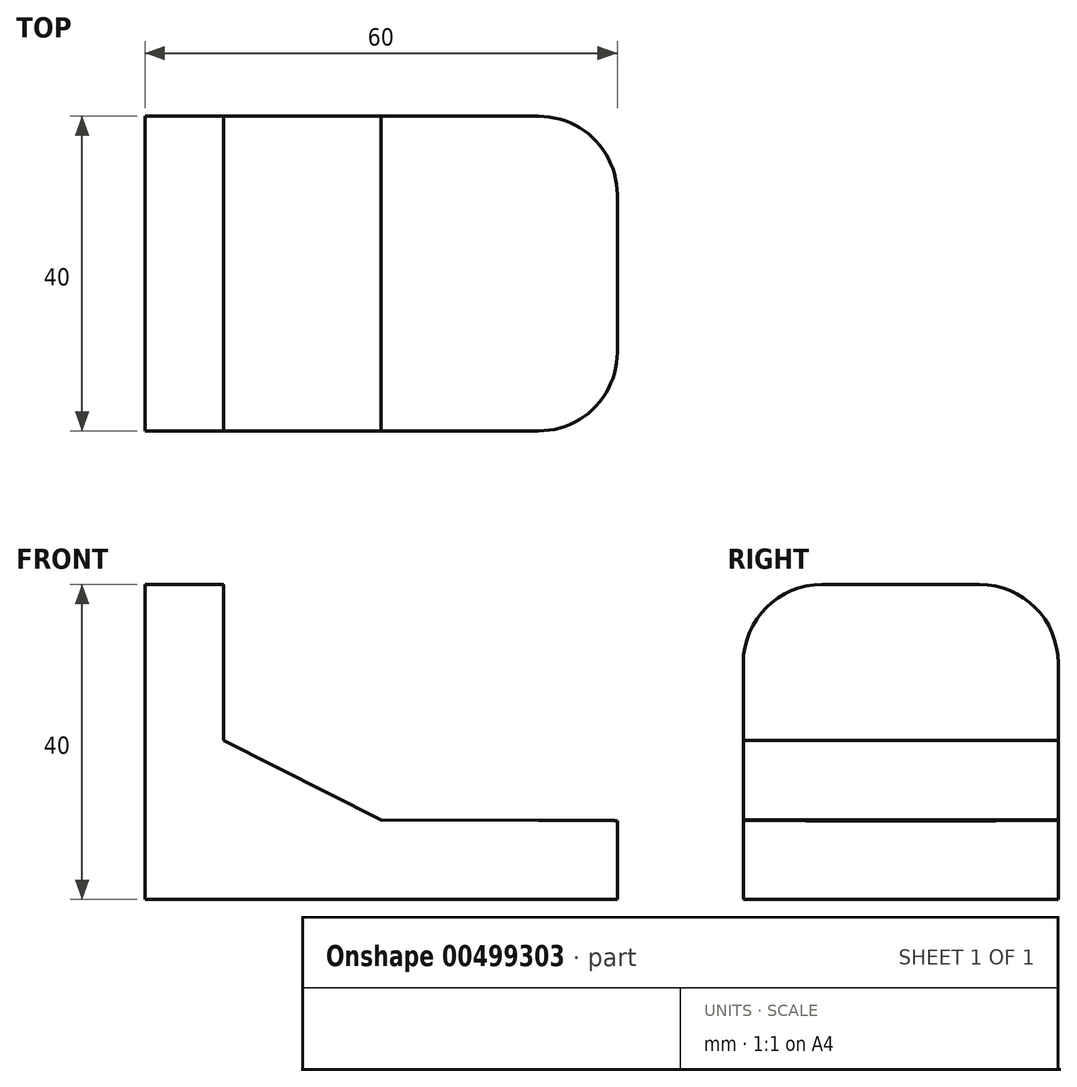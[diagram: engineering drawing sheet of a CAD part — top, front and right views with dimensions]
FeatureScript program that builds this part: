
annotation { "Feature Type Name" : "Feature", "Feature Type Description" : "" }
export const myFeature = defineFeature(function(context is Context, id is Id, definition is map)
    precondition{}
    {
        {
            var Q0;
            Q0=qCreatedBy(makeId("Front.planeOp"),FACE);
            var sketch = newSketch(context, id + "F0", { "sketchPlane" : qUnion([Q0])});
            skLineSegment(sketch, "E0", {"start": v(0, 0) * mm, "end": v(0, 40) * mm});
            skLineSegment(sketch, "E1", {"start": v(0, 40) * mm, "end": v(10, 40) * mm});
            skLineSegment(sketch, "E2", {"start": v(10, 40) * mm, "end": v(10, 20.21) * mm});
            skLineSegment(sketch, "E3", {"start": v(0, 0) * mm, "end": v(60, 0) * mm});
            skLineSegment(sketch, "E4", {"start": v(10, 20.21) * mm, "end": v(30, 10.13) * mm});
            skLineSegment(sketch, "E5", {"start": v(60, 0) * mm, "end": v(60, 10) * mm});
            skLineSegment(sketch, "E6", {"start": v(60, 10) * mm, "end": v(30, 10.13) * mm});
            skSolve(sketch);
        }
        {
            var Q0;
            Q0=makeQuery(id+"F0.imprint","IMPRINT",FACE,{"disambiguationData":[TD([[makeQuery(id+"F0.imprint","IMPRINT",EDGE,{"derivedFrom":sQuery(id+"F0.wireOp",EDGE,"E0")}),-1.0]])]});
            extrude(context, id + "F1", {"entities" : qUnion([Q0]), "depth" : 40 * mm});
        }
        {
            var Q0;
            Q0=makeQuery(id+"F1.opExtrude","CAP_EDGE",EDGE,{"disambiguationData":[OSD([sQuery(id+"F0.wireOp",EDGE,"E1")])],"isStart":true});
            var Q1;
            Q1=makeQuery(id+"F1.opExtrude","CAP_EDGE",EDGE,{"disambiguationData":[OSD([sQuery(id+"F0.wireOp",EDGE,"E1")])],"isStart":false});
            var Q2;
            Q2=makeQuery(id+"F1.opExtrude","CAP_EDGE",EDGE,{"disambiguationData":[OSD([sQuery(id+"F0.wireOp",EDGE,"E5")])],"isStart":false});
            var Q3;
            Q3=makeQuery(id+"F1.opExtrude","CAP_EDGE",EDGE,{"disambiguationData":[OSD([sQuery(id+"F0.wireOp",EDGE,"E5")])],"isStart":true});
            fillet(context, id + "F2", {"entities" : qUnion([Q0, Q1, Q2, Q3]), "radius" : 10 * mm, "tangentPropagation" : true, "allowEdgeOverflow" : false});
        }
    });
